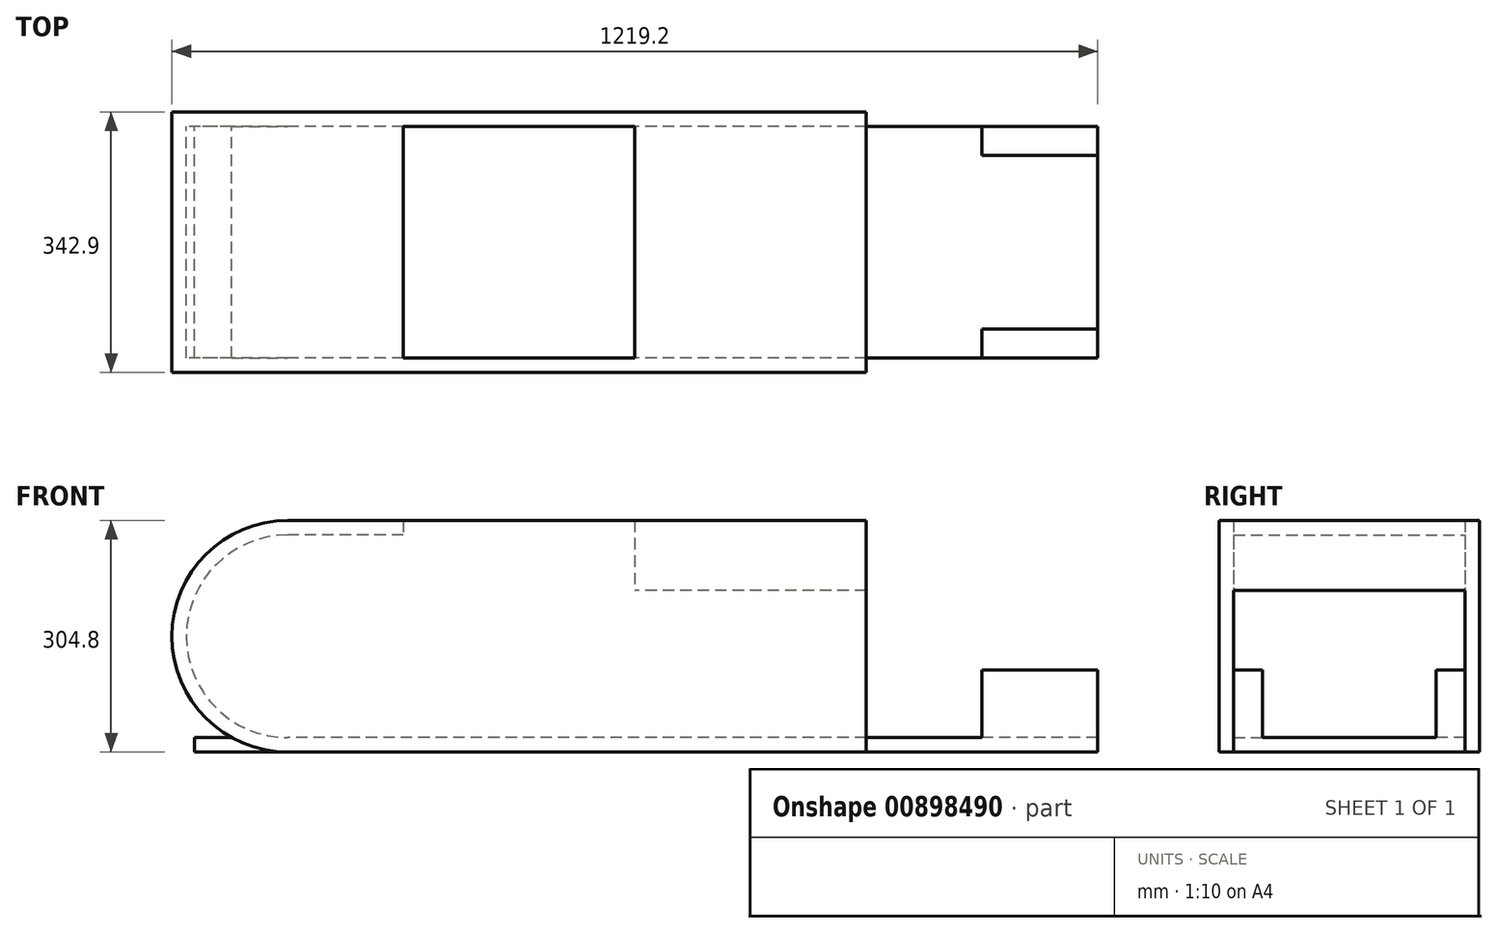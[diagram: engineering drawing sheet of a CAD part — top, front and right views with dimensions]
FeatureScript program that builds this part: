
annotation { "Feature Type Name" : "Feature", "Feature Type Description" : "" }
export const myFeature = defineFeature(function(context is Context, id is Id, definition is map)
    precondition{}
    {
        {
            var Q0;
            Q0=qCreatedBy(makeId("Front.planeOp"),FACE);
            var sketch = newSketch(context, id + "F0", { "sketchPlane" : qUnion([Q0])});
            skLineSegment(sketch, "E0.bottom", {"start": v(457.2, 152.4) * mm, "end": v(-457.2, 152.4) * mm});
            skLineSegment(sketch, "E0.top", {"start": v(457.2, -152.4) * mm, "end": v(-457.2, -152.4) * mm});
            skLineSegment(sketch, "E0.left", {"start": v(457.2, 152.4) * mm, "end": v(457.2, -152.4) * mm});
            skLineSegment(sketch, "E0.right", {"start": v(-457.2, 152.4) * mm, "end": v(-457.2, -152.4) * mm});
            skPoint(sketch, "E0.middle", {"position": v(0, 0) * mm});
            skCircle(sketch, "E1", {"center": v(-304.8, 0) * mm, "radius": 152.4 * mm});
            skSolve(sketch);
        }
        {
            var Q0;
            {var subQ0=sQuery(id+"F0.wireOp",EDGE,"E0.left");Q0=makeQuery(id+"F0.imprint","IMPRINT",FACE,{"disambiguationData":[TD([[makeQuery(id+"F0.imprint","IMPRINT",EDGE,{"derivedFrom":subQ0}),-1.0]])]});}
            var Q1;
            {var subQ0=sQuery(id+"F0.wireOp",EDGE,"E1");var subQ1=makeQuery(id+"F0.imprint","INTERSECT",VERTEX,{"derivedFrom":[sQuery(id+"F0.wireOp",EDGE,"E0.bottom"),subQ0]});Q1=makeQuery(id+"F0.imprint","IMPRINT",FACE,{"disambiguationData":[TD([[makeQuery(id+"F0.imprint","IMPRINT",EDGE,{"disambiguationData":[TD([[subQ1,-1.0]])],"derivedFrom":subQ0}),1.0]])]});}
            extrude(context, id + "F1", {"entities" : qUnion([Q0, Q1]), "depth" : 19.05 * mm, "offsetDistance" : 25.4 * mm});
        }
        {
            var Q0;
            Q0=makeQuery(id+"F1.opExtrude","CAP_FACE",FACE,{"disambiguationData":[OSD([sQuery(id+"F0.wireOp",EDGE,"E0.bottom"),sQuery(id+"F0.wireOp",EDGE,"E0.top"),sQuery(id+"F0.wireOp",EDGE,"E0.left"),sQuery(id+"F0.wireOp",EDGE,"E1")])],"isStart":false});
            var sketch = newSketch(context, id + "F2", { "sketchPlane" : qUnion([Q0])});
            skLineSegment(sketch, "E2.bottom", {"start": v(457.2, 152.4) * mm, "end": v(152.4, 152.4) * mm});
            skLineSegment(sketch, "E2.top", {"start": v(457.2, 60.32) * mm, "end": v(152.4, 60.32) * mm});
            skLineSegment(sketch, "E2.left", {"start": v(457.2, 152.4) * mm, "end": v(457.2, 60.32) * mm});
            skLineSegment(sketch, "E2.right", {"start": v(152.4, 152.4) * mm, "end": v(152.4, 60.32) * mm});
            skSolve(sketch);
        }
        {
            var Q0;
            Q0 = qSketchRegion(id + "F2", true);
            extrude(context, id + "F3", {"entities" : qUnion([Q0]), "operationType" : NewBodyOperationType.ADD, "depth" : 304.8 * mm, "offsetDistance" : 25.4 * mm});
        }
        {
            var Q0;
            Q0=makeQuery(id+"F3.opExtrude","CAP_FACE",FACE,{"disambiguationData":[OSD([sQuery(id+"F2.wireOp",EDGE,"E2.bottom"),sQuery(id+"F2.wireOp",EDGE,"E2.top"),sQuery(id+"F2.wireOp",EDGE,"E2.left"),sQuery(id+"F2.wireOp",EDGE,"E2.right")])],"isStart":false});
            var sketch = newSketch(context, id + "F4", { "sketchPlane" : qUnion([Q0])});
            skLineSegment(sketch, "E3.bottom", {"start": v(457.2, 152.4) * mm, "end": v(-457.2, 152.4) * mm});
            skLineSegment(sketch, "E3.top", {"start": v(457.2, -152.4) * mm, "end": v(-457.2, -152.4) * mm});
            skLineSegment(sketch, "E3.left", {"start": v(457.2, 152.4) * mm, "end": v(457.2, -152.4) * mm});
            skLineSegment(sketch, "E3.right", {"start": v(-457.2, 152.4) * mm, "end": v(-457.2, -152.4) * mm});
            skPoint(sketch, "E3.middle", {"position": v(0, 0) * mm});
            skCircle(sketch, "E4", {"center": v(-304.8, 0) * mm, "radius": 152.4 * mm});
            skSolve(sketch);
        }
        {
            var Q0;
            {var subQ0=sQuery(id+"F4.wireOp",EDGE,"E3.bottom");var subQ1=makeQuery(id+"F3.opExtrude","CAP_EDGE",EDGE,{"disambiguationData":[OSD([sQuery(id+"F2.wireOp",EDGE,"E2.right")])],"isStart":false});var subQ2=makeQuery(id+"F4.imprint","INTERSECT",VERTEX,{"derivedFrom":[subQ1,subQ0]});Q0=makeQuery(id+"F4.imprint","IMPRINT",FACE,{"disambiguationData":[TD([[makeQuery(id+"F4.imprint","IMPRINT",EDGE,{"disambiguationData":[TD([[subQ2,-1.0]])],"derivedFrom":subQ0}),1.0]])]});}
            var Q1;
            {var subQ0=sQuery(id+"F4.wireOp",EDGE,"E3.left");var subQ1=sQuery(id+"F4.wireOp",EDGE,"E3.top");var subQ2=makeQuery(id+"F4.imprint","INTERSECT",VERTEX,{"derivedFrom":[subQ1,subQ0]});Q1=makeQuery(id+"F4.imprint","IMPRINT",FACE,{"disambiguationData":[TD([[makeQuery(id+"F4.imprint","IMPRINT",EDGE,{"disambiguationData":[TD([[subQ2,-1.0]])],"derivedFrom":subQ1}),-1.0]])]});}
            var Q2;
            {var subQ0=sQuery(id+"F4.wireOp",EDGE,"E4");var subQ1=makeQuery(id+"F3.opExtrude","CAP_EDGE",EDGE,{"disambiguationData":[OSD([sQuery(id+"F2.wireOp",EDGE,"E2.right")])],"isStart":false});var subQ2=makeQuery(id+"F4.imprint","INTERSECT",VERTEX,{"derivedFrom":[subQ1,subQ0]});Q2=makeQuery(id+"F4.imprint","IMPRINT",FACE,{"disambiguationData":[TD([[makeQuery(id+"F4.imprint","IMPRINT",EDGE,{"disambiguationData":[TD([[subQ2,1.0]])],"derivedFrom":subQ0}),1.0]])]});}
            var Q3;
            {var subQ0=sQuery(id+"F4.wireOp",EDGE,"E3.left");var subQ7=sQuery(id+"F4.wireOp",EDGE,"E3.bottom");var subQ8=makeQuery(id+"F4.imprint","INTERSECT",VERTEX,{"derivedFrom":[subQ7,subQ0]});Q3=makeQuery(id+"F4.imprint","IMPRINT",FACE,{"disambiguationData":[TD([[makeQuery(id+"F4.imprint","IMPRINT",EDGE,{"disambiguationData":[TD([[subQ8,-1.0]])],"derivedFrom":subQ7}),1.0]])]});}
            var Q4;
            {var subQ0=sQuery(id+"F4.wireOp",EDGE,"E4");var subQ5=makeQuery(id+"F4.imprint","INTERSECT",VERTEX,{"derivedFrom":[sQuery(id+"F4.wireOp",EDGE,"E3.bottom"),subQ0]});Q4=makeQuery(id+"F4.imprint","IMPRINT",FACE,{"disambiguationData":[TD([[makeQuery(id+"F4.imprint","IMPRINT",EDGE,{"disambiguationData":[TD([[subQ5,1.0]])],"derivedFrom":subQ0}),1.0]])]});}
            extrude(context, id + "F5", {"entities" : qUnion([Q0, Q1, Q2, Q3, Q4]), "operationType" : NewBodyOperationType.ADD, "depth" : 19.05 * mm, "offsetDistance" : 25.4 * mm});
        }
        {
            var Q0;
            Q0=makeQuery(id+"F1.opExtrude","CAP_FACE",FACE,{"disambiguationData":[OSD([sQuery(id+"F0.wireOp",EDGE,"E0.bottom"),sQuery(id+"F0.wireOp",EDGE,"E0.top"),sQuery(id+"F0.wireOp",EDGE,"E0.left"),sQuery(id+"F0.wireOp",EDGE,"E1")])],"isStart":false});
            var sketch = newSketch(context, id + "F6", { "sketchPlane" : qUnion([Q0])});
            skLineSegment(sketch, "E5.bottom", {"start": v(-152.4, 152.4) * mm, "end": v(-304.8, 152.4) * mm});
            skLineSegment(sketch, "E5.top", {"start": v(-152.4, 133.35) * mm, "end": v(-304.8, 133.35) * mm});
            skLineSegment(sketch, "E5.left", {"start": v(-152.4, 152.4) * mm, "end": v(-152.4, 133.35) * mm});
            skLineSegment(sketch, "E5.right", {"start": v(-304.8, 152.4) * mm, "end": v(-304.8, 133.35) * mm});
            skCircle(sketch, "E6", {"center": v(-304.8, 0) * mm, "radius": 133.35 * mm});
            skLineSegment(sketch, "E7.bottom", {"start": v(762, -152.4) * mm, "end": v(-427.46, -152.4) * mm});
            skLineSegment(sketch, "E7.top", {"start": v(762, -133.35) * mm, "end": v(-427.46, -133.35) * mm});
            skLineSegment(sketch, "E7.left", {"start": v(762, -152.4) * mm, "end": v(762, -133.35) * mm});
            skLineSegment(sketch, "E7.right", {"start": v(-427.46, -152.4) * mm, "end": v(-427.46, -133.35) * mm});
            skCircle(sketch, "E8", {"center": v(-304.8, 0) * mm, "radius": 152.4 * mm});
            skSolve(sketch);
        }
        {
            var Q0;
            {var subQ3=sQuery(id+"F6.wireOp",EDGE,"E7.right");Q0=makeQuery(id+"F6.imprint","IMPRINT",FACE,{"disambiguationData":[TD([[makeQuery(id+"F6.imprint","IMPRINT",EDGE,{"derivedFrom":subQ3}),-1.0]])]});}
            var Q1;
            {var subQ0=sQuery(id+"F6.wireOp",EDGE,"E5.bottom");Q1=makeQuery(id+"F6.imprint","IMPRINT",FACE,{"disambiguationData":[TD([[makeQuery(id+"F6.imprint","IMPRINT",EDGE,{"derivedFrom":subQ0}),1.0]])]});}
            var Q2;
            {var subQ0=sQuery(id+"F6.wireOp",EDGE,"E5.right");Q2=makeQuery(id+"F6.imprint","IMPRINT",FACE,{"disambiguationData":[TD([[makeQuery(id+"F6.imprint","IMPRINT",EDGE,{"derivedFrom":subQ0}),1.0]])]});}
            var Q3;
            {var subQ0=sQuery(id+"F6.wireOp",EDGE,"E5.right");Q3=makeQuery(id+"F6.imprint","IMPRINT",FACE,{"disambiguationData":[TD([[makeQuery(id+"F6.imprint","IMPRINT",EDGE,{"derivedFrom":subQ0}),-1.0]])]});}
            var Q4;
            {var subQ0=sQuery(id+"F6.wireOp",EDGE,"E7.top");var subQ1=makeQuery(id+"F6.imprint","INTERSECT",VERTEX,{"derivedFrom":[sQuery(id+"F6.wireOp",EDGE,"E6"),subQ0]});Q4=makeQuery(id+"F6.imprint","IMPRINT",FACE,{"disambiguationData":[TD([[makeQuery(id+"F6.imprint","IMPRINT",EDGE,{"disambiguationData":[TD([[subQ1,1.0]])],"derivedFrom":subQ0}),1.0]])]});}
            var Q5;
            {var subQ3=sQuery(id+"F6.wireOp",EDGE,"E7.left");Q5=makeQuery(id+"F6.imprint","IMPRINT",FACE,{"disambiguationData":[TD([[makeQuery(id+"F6.imprint","IMPRINT",EDGE,{"derivedFrom":subQ3}),1.0]])]});}
            var Q6;
            {var subQ0=sQuery(id+"F6.wireOp",EDGE,"E7.bottom");var subQ1=makeQuery(id+"F1.opExtrude","CAP_EDGE",EDGE,{"disambiguationData":[OSD([sQuery(id+"F0.wireOp",EDGE,"E0.left")])],"isStart":false});var subQ2=makeQuery(id+"F6.imprint","INTERSECT",VERTEX,{"derivedFrom":[subQ1,subQ0]});Q6=makeQuery(id+"F6.imprint","IMPRINT",FACE,{"disambiguationData":[TD([[makeQuery(id+"F6.imprint","IMPRINT",EDGE,{"disambiguationData":[TD([[subQ2,-1.0]])],"derivedFrom":subQ0}),-1.0]])]});}
            var Q7;
            Q7=makeQuery(id+"F5.opExtrude","CAP_FACE",FACE,{"disambiguationData":[OSD([sQuery(id+"F4.wireOp",EDGE,"E3.bottom"),sQuery(id+"F4.wireOp",EDGE,"E3.top"),sQuery(id+"F4.wireOp",EDGE,"E3.left"),sQuery(id+"F4.wireOp",EDGE,"E4")])],"isStart":true});
            extrude(context, id + "F7", {"entities" : qUnion([Q0, Q1, Q2, Q3, Q4, Q5, Q6]), "operationType" : NewBodyOperationType.ADD, "endBound" : BoundingType.UP_TO_SURFACE, "depth" : 25.4 * mm, "endBoundEntityFace" : qUnion([Q7]), "offsetDistance" : 25.4 * mm});
        }
        {
            var Q0;
            {var subQ0=sQuery(id+"F6.wireOp",EDGE,"E7.top");var subQ1=makeQuery(id+"F6.imprint","INTERSECT",VERTEX,{"disambiguationData":[OD(1.0)],"derivedFrom":[subQ0,sQuery(id+"F6.wireOp",EDGE,"E8")]});Q0=makeQuery(id+"F7.opExtrude","SWEPT_FACE",FACE,{"disambiguationData":[OSD([subQ0]),TDD([makeQuery(id+"F6.imprint","IMPRINT",EDGE,{"disambiguationData":[TD([[makeQuery(id+"F6.imprint","INTERSECT",VERTEX,{"derivedFrom":[subQ0,sQuery(id+"F6.wireOp",EDGE,"E7.left")]}),-1.0]])],"derivedFrom":subQ0}),makeQuery(id+"F6.imprint","IMPRINT",EDGE,{"disambiguationData":[TD([[subQ1,1.0]])],"derivedFrom":subQ0}),makeQuery(id+"F6.imprint","IMPRINT",EDGE,{"disambiguationData":[TD([[makeQuery(id+"F6.imprint","INTERSECT",VERTEX,{"derivedFrom":[sQuery(id+"F6.wireOp",EDGE,"E6"),subQ0]}),1.0]])],"derivedFrom":subQ0})])]});}
            var sketch = newSketch(context, id + "F8", { "sketchPlane" : qUnion([Q0])});
            skLineSegment(sketch, "E9.bottom", {"start": v(762, -19.05) * mm, "end": v(609.6, -19.05) * mm});
            skLineSegment(sketch, "E9.top", {"start": v(762, -57.15) * mm, "end": v(609.6, -57.15) * mm});
            skLineSegment(sketch, "E9.left", {"start": v(762, -19.05) * mm, "end": v(762, -57.15) * mm});
            skLineSegment(sketch, "E9.right", {"start": v(609.6, -19.05) * mm, "end": v(609.6, -57.15) * mm});
            skLineSegment(sketch, "E10.bottom", {"start": v(762, -323.85) * mm, "end": v(609.6, -323.85) * mm});
            skLineSegment(sketch, "E10.top", {"start": v(762, -285.75) * mm, "end": v(609.6, -285.75) * mm});
            skLineSegment(sketch, "E10.left", {"start": v(762, -323.85) * mm, "end": v(762, -285.75) * mm});
            skLineSegment(sketch, "E10.right", {"start": v(609.6, -323.85) * mm, "end": v(609.6, -285.75) * mm});
            skSolve(sketch);
        }
        {
            var Q0;
            Q0 = qSketchRegion(id + "F8", true);
            extrude(context, id + "F9", {"entities" : qUnion([Q0]), "operationType" : NewBodyOperationType.ADD, "depth" : 88.9 * mm, "offsetDistance" : 25.4 * mm});
        }
    });
